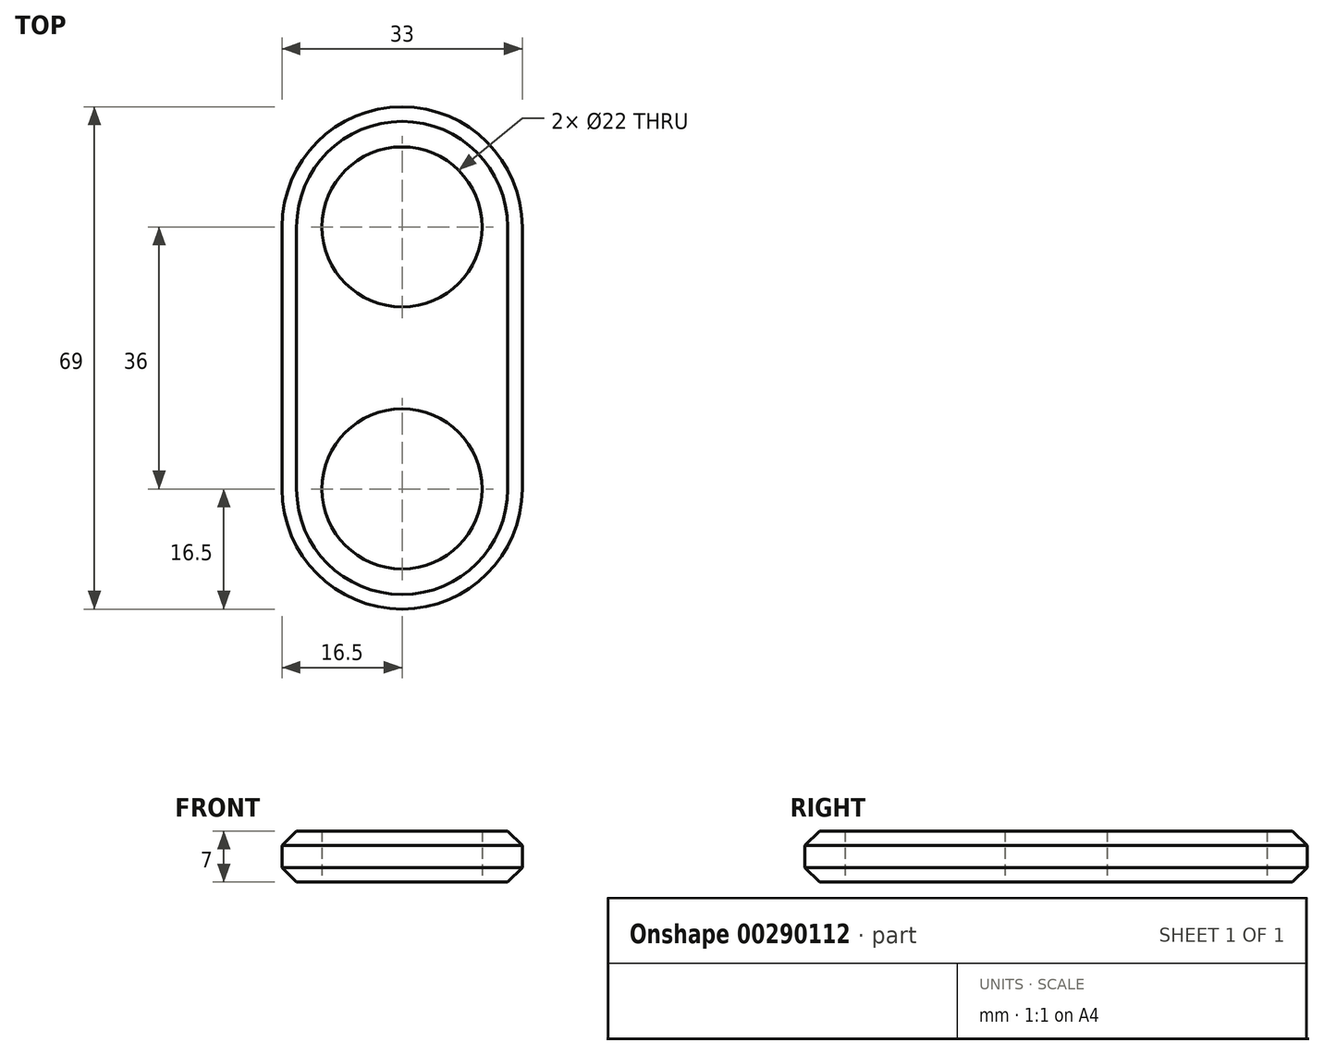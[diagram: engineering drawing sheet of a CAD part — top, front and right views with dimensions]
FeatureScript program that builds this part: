
annotation { "Feature Type Name" : "Feature", "Feature Type Description" : "" }
export const myFeature = defineFeature(function(context is Context, id is Id, definition is map)
    precondition{}
    {
        {
            var Q0;
            Q0=qCreatedBy(makeId("Top.planeOp"),FACE);
            var sketch = newSketch(context, id + "F0", { "sketchPlane" : qUnion([Q0])});
            skCircle(sketch, "E0", {"center": v(0, 0) * mm, "radius": 11 * mm});
            skCircle(sketch, "E1", {"center": v(0, 0) * mm, "radius": 16.5 * mm});
            skLineSegment(sketch, "E2", {"start": v(0, 0) * mm, "end": v(0, 36) * mm});
            skCircle(sketch, "E3", {"center": v(0, 36) * mm, "radius": 11 * mm});
            skCircle(sketch, "E4", {"center": v(0, 36) * mm, "radius": 16.5 * mm});
            skLineSegment(sketch, "E5", {"start": v(-16.5, 36) * mm, "end": v(-16.5, 0) * mm});
            skLineSegment(sketch, "E6", {"start": v(-16.5, 0) * mm, "end": v(16.5, 0) * mm});
            skLineSegment(sketch, "E7", {"start": v(16.5, 0) * mm, "end": v(16.5, 36) * mm});
            skSolve(sketch);
        }
        {
            var Q0;
            Q0 = qSketchRegion(id + "F0", true);
            extrude(context, id + "F1", {"entities" : qUnion([Q0]), "depth" : 7 * mm});
        }
        {
            var Q0;
            Q0=makeQuery(id+"F1.opExtrude","CAP_EDGE",EDGE,{"disambiguationData":[OSD([sQuery(id+"F0.wireOp",EDGE,"E7")])],"isStart":true});
            var Q1;
            Q1=makeQuery(id+"F1.opExtrude","CAP_EDGE",EDGE,{"disambiguationData":[OSD([sQuery(id+"F0.wireOp",EDGE,"E7")])],"isStart":false});
            chamfer(context, id + "F2", {"entities" : qUnion([Q0, Q1]), "width" : 2 * mm, "tangentPropagation" : true});
        }
    });
